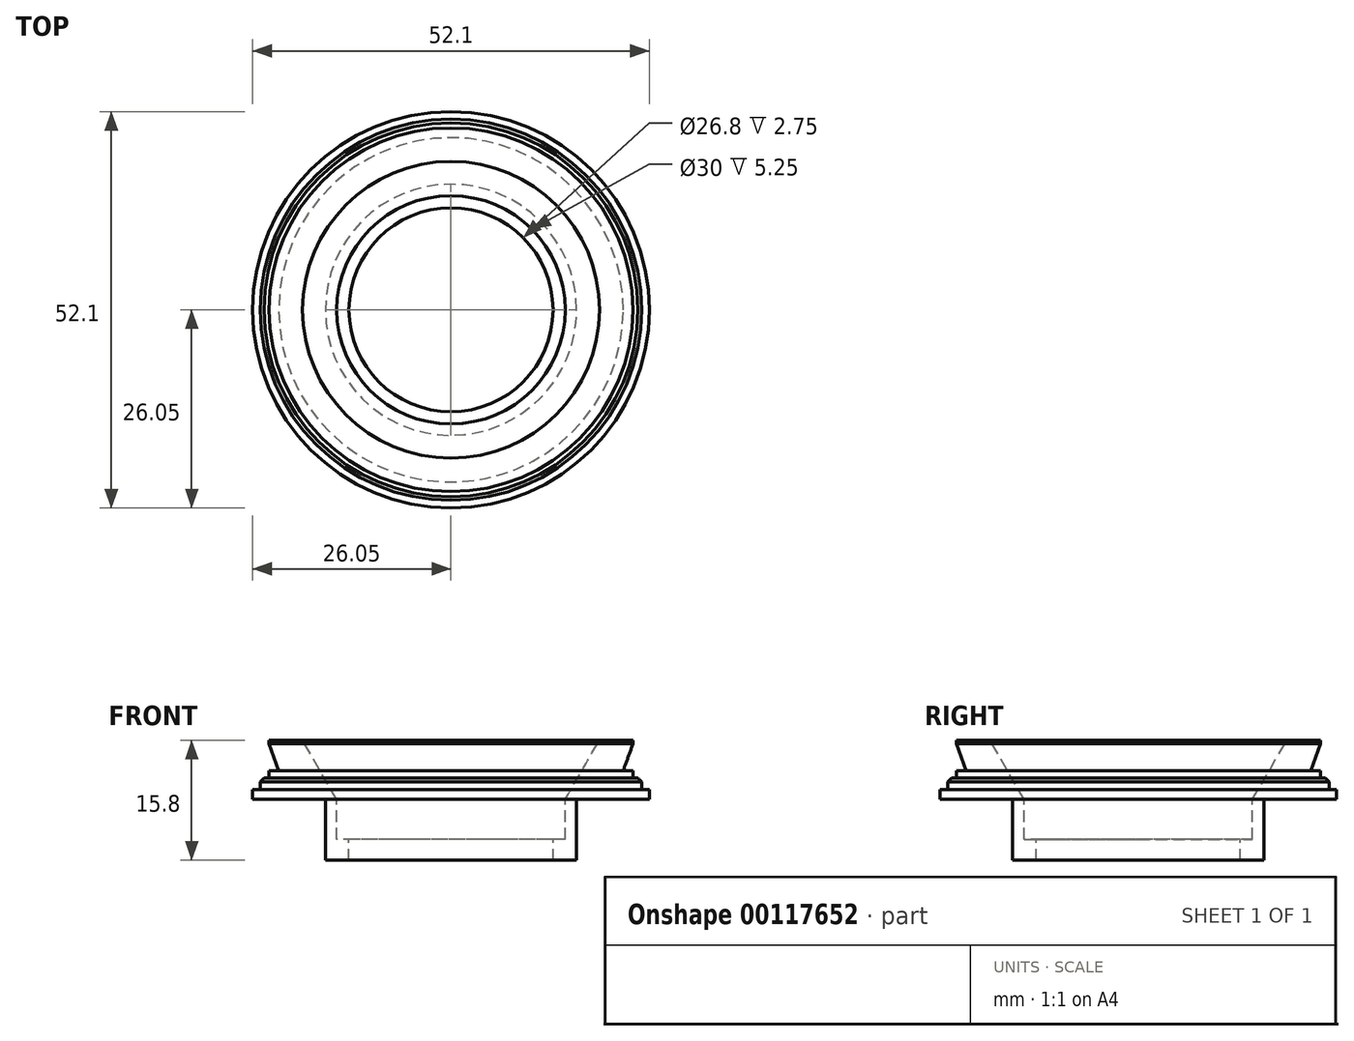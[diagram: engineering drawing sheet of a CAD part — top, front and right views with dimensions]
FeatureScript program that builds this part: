
annotation { "Feature Type Name" : "Feature", "Feature Type Description" : "" }
export const myFeature = defineFeature(function(context is Context, id is Id, definition is map)
    precondition{}
    {
        {
            var Q0;
            Q0=qCreatedBy(makeId("Front.planeOp"),FACE);
            var sketch = newSketch(context, id + "F0", { "sketchPlane" : qUnion([Q0])});
            skLineSegment(sketch, "E0", {"start": v(0, 0) * mm, "end": v(38.11, 0) * mm, "construction": true});
            skLineSegment(sketch, "E1", {"start": v(19.5, -34.5) * mm, "end": v(23.9, -34.5) * mm});
            skLineSegment(sketch, "E2", {"start": v(23.9, -34.5) * mm, "end": v(23.9, -35) * mm});
            skLineSegment(sketch, "E3", {"start": v(23.9, -35) * mm, "end": v(22.63, -38.5) * mm});
            skLineSegment(sketch, "E4", {"start": v(22.63, -38.5) * mm, "end": v(23.9, -38.5) * mm});
            skLineSegment(sketch, "E5", {"start": v(23.9, -38.5) * mm, "end": v(23.9, -39.5) * mm});
            skLineSegment(sketch, "E6", {"start": v(23.9, -39.5) * mm, "end": v(24.55, -39.5) * mm});
            skLineSegment(sketch, "E7", {"start": v(26.3, -52.3) * mm, "end": v(26.05, -52.3) * mm});
            skLineSegment(sketch, "E8", {"start": v(26.05, -42.3) * mm, "end": v(16.5, -42.3) * mm});
            skLineSegment(sketch, "E9", {"start": v(16.5, -42.3) * mm, "end": v(16.5, -50.3) * mm});
            skLineSegment(sketch, "E10", {"start": v(13.4, -50.3) * mm, "end": v(13.4, -47.55) * mm});
            skLineSegment(sketch, "E11", {"start": v(13.4, -47.55) * mm, "end": v(15, -47.55) * mm});
            skLineSegment(sketch, "E12", {"start": v(15, -47.55) * mm, "end": v(15, -42.3) * mm});
            skLineSegment(sketch, "E13", {"start": v(15, -42.3) * mm, "end": v(19.5, -34.5) * mm});
            skLineSegment(sketch, "E14", {"start": v(0, 0) * mm, "end": v(0, -18.86) * mm, "construction": true});
            skLineSegment(sketch, "E15", {"start": v(25.05, -40) * mm, "end": v(25.05, -41) * mm});
            skLineSegment(sketch, "E16", {"start": v(24.55, -39.5) * mm, "end": v(25.05, -40) * mm});
            skLineSegment(sketch, "E17.trimOffspring", {"start": v(16.5, -50.3) * mm, "end": v(13.4, -50.3) * mm});
            skLineSegment(sketch, "E18", {"start": v(25.05, -41) * mm, "end": v(26.05, -41) * mm});
            skLineSegment(sketch, "E19", {"start": v(26.05, -41) * mm, "end": v(26.05, -42.3) * mm});
            skPoint(sketch, "E20.orphan", {"position": v(25.05, -42.3) * mm});
            skSolve(sketch);
        }
        {
            var Q0;
            Q0=makeQuery(id+"F0.imprint","IMPRINT",FACE,{"disambiguationData":[TD([[makeQuery(id+"F0.imprint","IMPRINT",EDGE,{"derivedFrom":sQuery(id+"F0.wireOp",EDGE,"E1")}),-1.0]])]});
            var Q1;
            Q1=sQuery(id+"F0.wireOp",EDGE,"E14");
            revolve(context, id + "F1", {"entities" : qUnion([Q0]), "axis" : qUnion([Q1]), "revolveType" : RevolveType.FULL});
        }
    });
